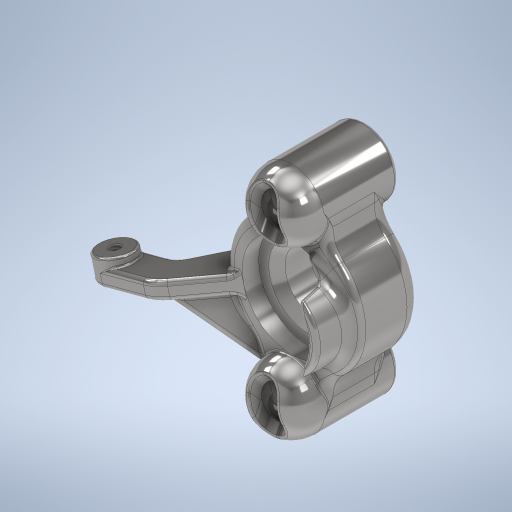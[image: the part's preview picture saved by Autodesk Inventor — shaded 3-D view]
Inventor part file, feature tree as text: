
AUTODESK INVENTOR PART (.ipt)
format: ipt  version: 2024 (Build 280153000, 153)  size: 2,001,920 bytes
history: native  units: in
note: dims shown in document units (in); Inventor stores cm internally (conversion verified against a paired STEP export)
features: fillet x21, sketch x14, extrude x9, projected_geometry x6, plane x4, other x4, revolve x3, thread x3, chamfer x2, mirror x1, hole x1, rib x1, draft x1, direct_edit x1
ambient origin geometry x8: Origin, YZ Plane, XZ Plane, XY Plane, X Axis, Y Axis, Z Axis, Center Point
bodies: Solid1 (feature_tree)
feature tree (71):
  extrude  "Extrusion1"  Depth=0.5in
  fillet  "Fillet1"  Radius=0.5in
  revolve  "Revolution1"  [1 undecoded]
  mirror  "Mirror1"
  extrude  "Extrusion2"  TaperAngle=90.0deg  [1 undecoded]
  extrude  "Extrusion3"  Depth=0.125in TaperAngle=0.0deg
  plane  "Work Plane1"
  plane  "Work Plane3"
  extrude  "Extrusion4"  Depth=0.1875in TaperAngle=0.0deg
  revolve  "Revolution2"  Angle=15.0deg
  revolve  "Revolution3"  [1 undecoded]
  fillet  "Fillet2"  Radius=0.215in
  extrude  "Extrusion5"  Depth=0.215in
  chamfer  "Chamfer1"  Distance=0.0625in
  extrude  "Extrusion6"  Depth=0.475in
  fillet  "Fillet3"  [1 undecoded]
  fillet  "Fillet4"  Radius=0.015in
  fillet  "Fillet5"  Radius=0.0625in
  fillet  "Fillet6"  Radius=0.015in
  chamfer  "Chamfer2"  Distance=0.0625in Angle=45.0deg
  thread  "Thread1"  [1 undecoded]
  thread  "Thread2"  [1 undecoded]
  thread  "Thread3"  [1 undecoded]
  fillet  "Fillet7"  Radius=0.125in
  fillet  "Fillet8"  Radius=0.032in
  fillet  "Fillet9"  Radius=0.032in
  extrude  "Extrusion7"  Depth=1.2in
  fillet  "Fillet10"  Radius=0.135in
  fillet  "Fillet11"  Radius=0.15in
  fillet  "Fillet12"  [1 undecoded]
  extrude  "Extrusion8"  Depth=0.032in
  fillet  "Fillet13"  Radius=0.25in
  hole  "Hole2"  [1 undecoded]
  fillet  "Fillet14"  Radius=0.0625in
  plane  "Work Plane4"
  rib  "Rib1"
  fillet  "Fillet15"  Radius=0.032in
  fillet  "Fillet16"  Radius=0.015in
  extrude  "Extrusion9"  Depth=0.1in
  draft  "FaceDraft1"
  fillet  "Fillet17"  Radius=0.05in
  fillet  "Fillet18"  Radius=0.05in
  fillet  "Fillet19"  Radius=0.315in
  fillet  "Fillet20"  Radius=0.25in
  fillet  "Fillet21"  Radius=0.0172in
  direct_edit  "Direct Edit1"
  sketch  "Sketch1"  dims[d0=1.7625in d1=0.5in d2=0.5in]
  sketch  "Sketch2"  dims[d3=0.5625in d4=0.0in d5=0.25in]
  sketch  "Sketch3"  dims[d6=0.325in d7=90.0deg]
  sketch  "Sketch4"  dims[d8=0.75in d9=0.125in d10=0.0in]
  other  "Work Axis1"
  other  "Work Axis2"
  plane  "Work Plane2"
  other  "Work Axis3"
  sketch  "Sketch5"  dims[d11=0.5in d12=0.1875in d13=0.0in]
  sketch  "Sketch6"  dims[d14=15.0deg d15=15.0deg]
  sketch  "Sketch7"  dims[d16=0.0in d17=0.0in d18=0.0in d19=0.215in]
  sketch  "Sketch8"  dims[d20=0.6871in d21=0.215in]
  sketch  "Sketch9"  dims[d22=0.6871in]
  sketch  "Sketch10"  dims[d23=0.1in d24=0.0625in d25=0.0in]
  sketch  "Sketch11"  dims[d26=0.015in d27=0.125in d28=45.0deg d29=0.475in d30=0.0in d31=0.0in d32=0.015in d33=0.0625in d34=0.015in]
  sketch  "Sketch13"  dims[d35=0.014in d36=0.0625in d37=0.125in d38=45.0deg d39=0.315in d40=0.0in d41=0.315in d42=0.0in d43=0.315in d44=0.0in d45=0.125in d46=0.032in d47=0.032in]
  sketch  "Sketch14"  dims[d48=0.3779in d52=1.2in d53=0.135in d54=0.15in d55=15.0deg]
  sketch  "Sketch15"  dims[d56=0.125in d57=0.0in d58=0.032in d59=0.25in d60=0.125in d61=0.0625in d62=0.0in d63=0.032in d71=0.0849in d72=0.75in d73=0.2362in d74=0.1181in d75=0.5635in d76=0.75in d77=0.8108in d78=0.015in d79=0.1in d80=0.1in d81=0.0in d82=0.0in d83=0.1in d84=0.1in d85=0.05in d86=0.05in d87=0.315in d88=0.25in d89=0.0in d90=0.0172in d91=0.125in d92=0.032in d93=0.015in d94=0.015in d95=0.015in d96=3.937in d97=0.3937in d98=0.3937in d64=1.0in d65=1.0in d66=1.0in d67=0.15in d68=0.25in d69=0.375in d70=0.5635in]
  projected_geometry  "Project Cut Edges1"
  projected_geometry  "Project Cut Edges2"
  projected_geometry  "Project Cut Edges3"
  projected_geometry  "Project Cut Edges4"
  projected_geometry  "Project Cut Edges5"
  projected_geometry  "Project Cut Edges6"
  other  "Scale1"
note: 9 required parameter values undecoded (feature->parameter linkage not recoverable at this tier; creation-order binding heuristic only, values carry confidence <= 0.55)